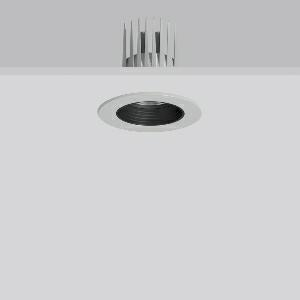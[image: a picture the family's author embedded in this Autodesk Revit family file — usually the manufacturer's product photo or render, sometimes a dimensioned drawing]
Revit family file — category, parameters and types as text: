
# Revit family: heledon_mini_e_901755_004_3_a475
name_source: partatom
category: Lighting Fixtures
units: mm (PartAtom-declared; Revit-internal decimal feet)

## family parameters
Cut with Voids When Loaded = No
Host = Face
Light Source = No
Part Type = Normal
Room Calculation Point = No
Round Connector Dimension = Use Diameter
Shared = No

## types (1)
- HELEDON mini E (1 x LED Modul 935, 2800 lm, 3500)
    Apparent Load = 29 VA
    Approval mark = CE
    CIE Flux Codes = 95 100 100 100 100
    Color Rendering = 92
    Color Temperature = 3500
    Default Elevation = 1800 mm
    Description = Series: HELEDON mini
Round recessed downlight. Housing: die-cast aluminium, powder-coated. Black plastic ring and recessed LED to prevent glare from the side. Optical assembly with lens made of plastic (polycarbonate) for the best homogeneous light distribution - can be changed without tools. Best colour rendering index Ra>90. Suitable for Recessed ceiling mounting. Installation without tools thanks to spring fastening system. Including separate LED converter with connecting cable 600 mm.High quality converter without flickering and stroboscopic effect. Through-wiring box (5 pole) available as accessory. The following accessories can be mounted without use of tools: interchangeable lenses, decorative glasses, honeycomb louvre, clear and frosted diffusers, white interchangeable plastic ring. 
Colour: silver
Diameter: 124 mm
Height: 3 mm
Cut-out diameter: 114 mm
Recess height: 170 mm
Luminaire: recess height: 120 mm
Lamp: LED
Socket: without socket
Colour temperature: 3500K
Colour rendering index (CRI): 92
System power: 29 W
Rated luminous flux: 2800 lm
Luminous efficiency: 97 lm/W
Control gear: Regulated power supply
Protection class: II
Type of protection: IP 20
    Height = 0 mm  [stored 0 ft]
    Lamp = 1 x LED Modul 935
    Lamp Light Flux = 2800 lm
    Lamp count = 1
    Length = 124 mm  [stored 0.406824 ft]
    Lifetime = 50000 h
    Luminous efficacy = 97 lm/W
    Manufacturer = RZB
    ModVariant = No
    Model = 901755.004.3
    Mounting Place = Ceiling
    Mounting Type = Recessed
    Number of Poles = 1
    OnlyDefault = Yes
    Power Factor = 1
    Product Name = HELEDON mini E
    Product group = Recessed downlights
    ProductGroupID = 402
    Protection Class = Protection class II
    Protection Degree = IP 20
    RLX_Detail_Level = 1
    RLX_Emergency_Light_Flux = 0 lm
    RLX_Emergency_Type = 0
    RLX_Emergency_Type_DB = No
    RlxData = <blob elided: 133173 chars, md5=f64eb14c>
    Socket = socket
    Standby Power = 0 W
    System Light Flux = 2800 lm
    System Power = 29 W
    Type Comments = Product without accessories
    Type Image = 901656.004.jpg
    URL = http://relux.com
    VarID = ---
    Voltage = 230 V
    Voltage Range = 220-240 V
    Weight = 0.00 kg
    Width = 0 mm  [stored 0 ft]

note: [stored X ft] marks values corroborated as IEEE doubles in the binary element streams (Revit-internal decimal feet)

## geometry (parser evidence)
native form markers: Blend x4, Sweep x9
no freeform markers — native parametric forms only
